# Revit family: IS_Prosys_E2332_BIM_NL
name_source: partatom
category: Plumbing Fixtures
units: mm (PartAtom-declared; Revit-internal decimal feet)

## family parameters
Cut with Voids When Loaded = No
Host = Face
OmniClass Number = 23.45.05.21.11.11
OmniClass Title = Water Operated Water Closets
Part Type = Normal
Room Calculation Point = No
Round Connector Dimension = Use Diameter
Shared = Yes

## types (2) — shared parameters
Accessories = https://www.idealstandard.nl
AreaUnits = millimeters
Assembly Code = C1030200
AssetType = Fixed
BIMObjectName = IS_IdealStandard_WCpanbackrests_Prosys_E2332
BREEAMApproved = No
Brand = Ideal Standrad
ConnectionType = Plumbing
Description = PROSYS ECO WC FRAME CLASS 1 300MM WIDE X 1150MM HIGH MECHANICAL
DurationUnit = year
ECA = No
ExpectedLife = 30
Features = WC FRAME CLASS 1 300MM WIDE X 1150MM HIGH MECHANICAL
Help = https://www.idealstandard.nl
IfcExportAs = IfcSanitaryTerminalType
IfcExportType = CISTERN
InstallationInstructions = https://www.idealstandard.nl
LinearUnits = millimeters
Manufacturer = https://www.idealstandard.nl
ManufacturerURL = www.idealstandard.nl
ModelReference = PROSYS ECO WC FRAME CLASS 1 300MM WIDE X 1150MM HIGH MECHANICAL
NBSDescription = WC pan backrests
NBSReference = 45-35-72/382
Name = WCpanbackrests_Prossys_R0279_IdealStandard
NettWeight = 11.50 Kg
NominalDepth = 190 mm
NominalHeight = 1082 mm
NominalLength = 190 mm
NominalWidth = 300 mm
ProductInformation = https://www.idealstandard.nl
Shape = Sculptured
Size = 300 x 190 x 1082 mm
Space = Internal
ToiletPanType = WashDown
ToiletType = Other
URL = www.idealstandard.nl
Uniclass2 = Pr_40_20_93_89
Uniclass2015Code = Pr_40_20_76_98
Uniclass2015Description = WC pan backrests
Uniclass2015Reference = Pr_40_20_76_98
Uniclass2015Title = WC pan backrests
Uniclass2015Version = V1.20
Version = 1
VolumeUnits = Litres
WRAS = No
WarrantyDescription = Manufacturers Warranty
WarrantyDurationParts = 5
WarrantyDurationUnit = year
WarrantyGuarantorParts = https://www.idealstandard.nl
WaterEfficientProduct = No
zero-valued in all types: CWFU, Cost, Default Elevation, HWFU, SpilloverLevel, WFU

## per-type parameters (varying)
| type | BarCode | Finish | FlushPlate_Material | Model | ModelNumber |
| E2332AA - ECO WC FRAME CL1 OLEAS M2 CHROME F/PLATE | 3391500584082 | Chrome | Chrome_Polished | E2332AA | E2332AA |
| E2332AC - ECO WC FRAME CL1 OLEAS M2 WHITE F/PLATE | 3391500584099 | White | PVC_White | E2332AC | E2332AC |

## geometry (parser evidence)
native form markers: Sweep x2
no freeform markers — native parametric forms only
